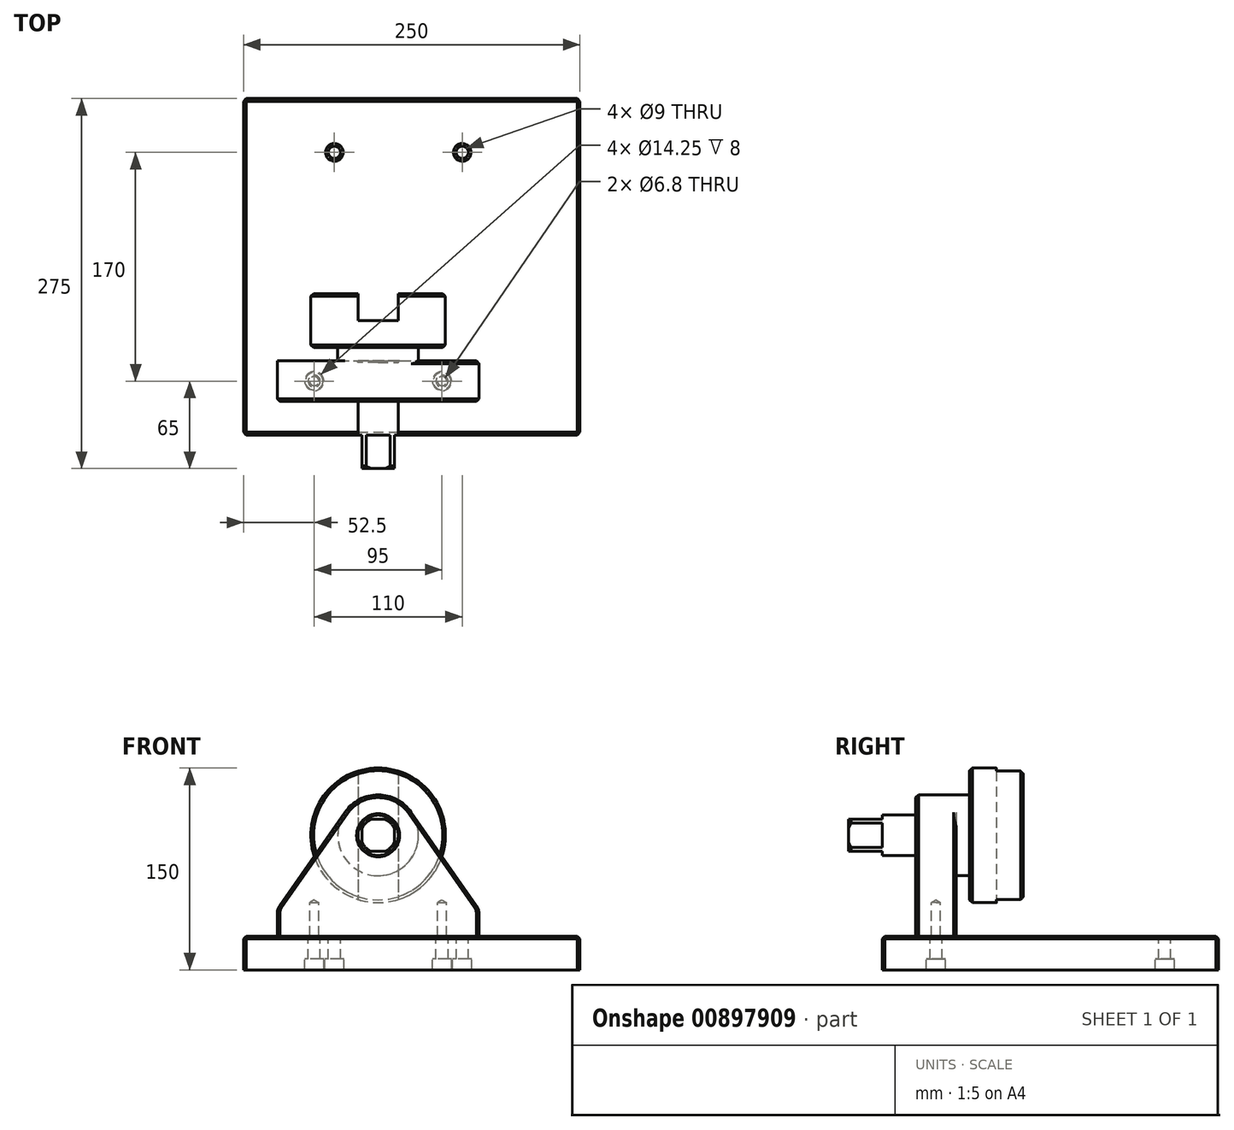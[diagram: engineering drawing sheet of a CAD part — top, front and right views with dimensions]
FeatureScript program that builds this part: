
annotation { "Feature Type Name" : "Feature", "Feature Type Description" : "" }
export const myFeature = defineFeature(function(context is Context, id is Id, definition is map)
    precondition{}
    {
        {
            var Q0;
            Q0=qCreatedBy(makeId("Top.planeOp"),FACE);
            cPlane(context, id + "F0", {"entities" : qUnion([Q0]), "cplaneType" : CPlaneType.OFFSET, "offset" : 25 * mm, "oppositeDirection" : true, "width" : 150 * mm, "height" : 150 * mm});
        }
        {
            var Q0;
            Q0=qCreatedBy(makeId("Front.planeOp"),FACE);
            var sketch = newSketch(context, id + "F1", { "sketchPlane" : qUnion([Q0])});
            skArc(sketch, "E0", {"start": v(24.6, 92.18) * mm, "mid": v(0, 105) * mm, "end": v(-24.6, 92.18) * mm});
            skLineSegment(sketch, "E1", {"start": v(-24.6, 92.18) * mm, "end": v(-75, 20) * mm});
            skLineSegment(sketch, "E2", {"start": v(-75, 20) * mm, "end": v(-75, 0) * mm});
            skLineSegment(sketch, "E3", {"start": v(-75, 0) * mm, "end": v(75, 0) * mm});
            skLineSegment(sketch, "E4", {"start": v(75, 0) * mm, "end": v(75, 20) * mm});
            skLineSegment(sketch, "E5", {"start": v(75, 20) * mm, "end": v(24.6, 92.18) * mm});
            skCircle(sketch, "E6", {"center": v(0, 75) * mm, "radius": 15 * mm});
            skSolve(sketch);
        }
        {
            var Q0;
            Q0=makeQuery(id+"F1.imprint","IMPRINT",FACE,{"disambiguationData":[TD([[makeQuery(id+"F1.imprint","IMPRINT",EDGE,{"derivedFrom":sQuery(id+"F1.wireOp",EDGE,"E0")}),1.0]])]});
            extrude(context, id + "F2", {"entities" : qUnion([Q0]), "depth" : 30 * mm, "offsetDistance" : 25 * mm});
        }
        {
            var Q0;
            Q0=makeQuery(id+"F2.opExtrude","SWEPT_EDGE",EDGE,{"disambiguationData":[OSD([sQuery(id+"F1.wireOp",EDGE,"E4"),sQuery(id+"F1.wireOp",EDGE,"E5")])]});
            var Q1;
            Q1=makeQuery(id+"F2.opExtrude","SWEPT_EDGE",EDGE,{"disambiguationData":[OSD([sQuery(id+"F1.wireOp",EDGE,"E1"),sQuery(id+"F1.wireOp",EDGE,"E2")])]});
            fillet(context, id + "F3", {"entities" : qUnion([Q0, Q1]), "radius" : 10 * mm, "tangentPropagation" : true, "allowEdgeOverflow" : false});
        }
        {
            var Q0;
            Q0=makeQuery(id+"F2.opExtrude","CAP_EDGE",EDGE,{"disambiguationData":[OSD([sQuery(id+"F1.wireOp",EDGE,"E6")])],"isStart":false});
            var Q1;
            Q1=makeQuery(id+"F2.opExtrude","CAP_EDGE",EDGE,{"disambiguationData":[OSD([sQuery(id+"F1.wireOp",EDGE,"E6")])],"isStart":true});
            chamfer(context, id + "F4", {"entities" : qUnion([Q0, Q1]), "width" : 1 * mm, "tangentPropagation" : true});
        }
        {
            var Q0;
            Q0=qCreatedBy(makeId("Top.planeOp"),FACE);
            var sketch = newSketch(context, id + "F5", { "sketchPlane" : qUnion([Q0])});
            skLineSegment(sketch, "E7.bottom", {"start": v(-100, -55) * mm, "end": v(150, -55) * mm});
            skLineSegment(sketch, "E7.top", {"start": v(-100, 195) * mm, "end": v(150, 195) * mm});
            skLineSegment(sketch, "E7.left", {"start": v(-100, -55) * mm, "end": v(-100, 195) * mm});
            skLineSegment(sketch, "E7.right", {"start": v(150, -55) * mm, "end": v(150, 195) * mm});
            skLineSegment(sketch, "E8", {"start": v(0, 0) * mm, "end": v(15, 170) * mm, "construction": true});
            skSolve(sketch);
        }
        {
            var Q0;
            Q0=makeQuery(id+"F5.imprint","IMPRINT",FACE,{"disambiguationData":[TD([[makeQuery(id+"F5.imprint","IMPRINT",EDGE,{"derivedFrom":sQuery(id+"F5.wireOp",EDGE,"E7.bottom")}),1.0]])]});
            var Q1;
            Q1=qCreatedBy(id+"F0.planeOp",FACE);
            extrude(context, id + "F6", {"entities" : qUnion([Q0]), "endBound" : BoundingType.UP_TO_SURFACE, "oppositeDirection" : true, "depth" : 25 * mm, "endBoundEntityFace" : qUnion([Q1]), "offsetDistance" : 25 * mm});
        }
        {
            var Q0;
            Q0=qCreatedBy(id+"F0.planeOp",FACE);
            var sketch = newSketch(context, id + "F7", { "sketchPlane" : qUnion([Q0])});
            skLineSegment(sketch, "E9.0", {"start": v(-75, -30) * mm, "end": v(75, -30) * mm, "construction": true});
            skLineSegment(sketch, "E9.1", {"start": v(-75, 0) * mm, "end": v(75, 0) * mm, "construction": true});
            skLineSegment(sketch, "E9.2", {"start": v(-75, -30) * mm, "end": v(-75, 0) * mm, "construction": true});
            skLineSegment(sketch, "E9.3", {"start": v(75, -30) * mm, "end": v(75, 0) * mm, "construction": true});
            skLineSegment(sketch, "E10", {"start": v(-75, -15) * mm, "end": v(75, -15) * mm, "construction": true});
            skPoint(sketch, "E11", {"position": v(-47.5, -15) * mm});
            skPoint(sketch, "E12", {"position": v(47.5, -15) * mm});
            skLineSegment(sketch, "E13.0", {"start": v(0, 0) * mm, "end": v(15, 170) * mm, "construction": true});
            skLineSegment(sketch, "E14.bottom", {"start": v(90, 140) * mm, "end": v(-60, 140) * mm, "construction": true});
            skLineSegment(sketch, "E14.top", {"start": v(90, 170) * mm, "end": v(-60, 170) * mm, "construction": true});
            skLineSegment(sketch, "E14.left", {"start": v(90, 140) * mm, "end": v(90, 170) * mm, "construction": true});
            skLineSegment(sketch, "E14.right", {"start": v(-60, 140) * mm, "end": v(-60, 170) * mm, "construction": true});
            skLineSegment(sketch, "E15", {"start": v(90, 155) * mm, "end": v(-60, 155) * mm, "construction": true});
            skPoint(sketch, "E16", {"position": v(62.5, 155) * mm});
            skPoint(sketch, "E17", {"position": v(-32.5, 155) * mm});
            skLineSegment(sketch, "E18", {"start": v(15, 170) * mm, "end": v(15, 140) * mm, "construction": true});
            skSolve(sketch);
        }
        {
            var Q0;
            Q0=sQuery(id+"F7.wireOp",VERTEX,"E11");
            var Q1;
            Q1=sQuery(id+"F7.wireOp",VERTEX,"E12");
            var Q2;
            Q2=makeQuery(id+"F2.opExtrude","SWEPT_BODY",BODY,{"disambiguationData":[OSD([sQuery(id+"F1.wireOp",EDGE,"E0"),sQuery(id+"F1.wireOp",EDGE,"E1"),sQuery(id+"F1.wireOp",EDGE,"E2"),sQuery(id+"F1.wireOp",EDGE,"E3"),sQuery(id+"F1.wireOp",EDGE,"E4"),sQuery(id+"F1.wireOp",EDGE,"E5"),sQuery(id+"F1.wireOp",EDGE,"E6")])]});
            var Q3;
            Q3=makeQuery(id+"F6.opExtrude","SWEPT_BODY",BODY,{"disambiguationData":[OSD([sQuery(id+"F5.wireOp",EDGE,"E7.bottom"),sQuery(id+"F5.wireOp",EDGE,"E7.top"),sQuery(id+"F5.wireOp",EDGE,"E7.left"),sQuery(id+"F5.wireOp",EDGE,"E7.right")])]});
            hole(context, id + "F8", {"style" : HoleStyle.C_BORE, "endStyle" : HoleEndStyle.BLIND_IN_LAST, "oppositeDirection" : true, "standardTappedOrClearance" : lookupTablePath({ "fit" : "Normal", "standard" : "ISO", "engagement" : "75%", "pitch" : "1.25 mm", "size" : "M8", "type" : "Clearance & tapped" }), "standardBlindInLast" : lookupTablePath({ "fit" : "Normal", "standard" : "ISO", "engagement" : "75%", "pitch" : "1.25 mm", "size" : "M8", "type" : "Clearance & tapped" }), "holeDiameter" : 9 * mm, "cBoreDiameter" : 14.25 * mm, "cBoreDepth" : 8 * mm, "tapDrillDiameter" : 6.8 * mm, "majorDiameter" : 8 * mm, "showTappedDepth" : true, "holeDepth" : 25 * mm, "isTappedThrough" : true, "tappedDepth" : 21.25 * mm, "tapClearance" : 3, "startFromSketch" : true, "locations" : qUnion([Q0, Q1]), "scope" : qUnion([Q2, Q3])});
        }
        {
            var Q0;
            Q0=sQuery(id+"F7.wireOp",VERTEX,"E16");
            var Q1;
            Q1=sQuery(id+"F7.wireOp",VERTEX,"E17");
            var Q2;
            Q2=makeQuery(id+"F6.opExtrude","SWEPT_BODY",BODY,{"disambiguationData":[OSD([sQuery(id+"F5.wireOp",EDGE,"E7.bottom"),sQuery(id+"F5.wireOp",EDGE,"E7.top"),sQuery(id+"F5.wireOp",EDGE,"E7.left"),sQuery(id+"F5.wireOp",EDGE,"E7.right")])]});
            hole(context, id + "F9", {"style" : HoleStyle.C_BORE, "endStyle" : HoleEndStyle.THROUGH, "oppositeDirection" : true, "standardTappedOrClearance" : lookupTablePath({ "fit" : "Normal", "standard" : "ISO", "size" : "M8", "type" : "Clearance" }), "standardBlindInLast" : lookupTablePath({ "fit" : "Normal", "standard" : "ISO", "size" : "M8", "type" : "Clearance" }), "holeDiameter" : 9 * mm, "cBoreDiameter" : 14.25 * mm, "cBoreDepth" : 8 * mm, "majorDiameter" : 8 * mm, "isTappedThrough" : true, "tappedDepth" : 21.25 * mm, "tapClearance" : 3, "startFromSketch" : true, "locations" : qUnion([Q0, Q1]), "scope" : qUnion([Q2])});
        }
        {
            var Q0;
            Q0=makeQuery(id+"F2.opExtrude","CAP_FACE",FACE,{"disambiguationData":[OSD([sQuery(id+"F1.wireOp",EDGE,"E0"),sQuery(id+"F1.wireOp",EDGE,"E1"),sQuery(id+"F1.wireOp",EDGE,"E2"),sQuery(id+"F1.wireOp",EDGE,"E3"),sQuery(id+"F1.wireOp",EDGE,"E4"),sQuery(id+"F1.wireOp",EDGE,"E5"),sQuery(id+"F1.wireOp",EDGE,"E6")])],"isStart":true});
            var sketch = newSketch(context, id + "F10", { "sketchPlane" : qUnion([Q0])});
            skCircle(sketch, "E19.0", {"center": v(0, 75) * mm, "radius": 15 * mm});
            skCircle(sketch, "E20", {"center": v(0, 75) * mm, "radius": 50 * mm});
            skCircle(sketch, "E21", {"center": v(0, 75) * mm, "radius": 30 * mm});
            skSolve(sketch);
        }
        {
            var Q0;
            Q0=makeQuery(id+"F10.imprint","IMPRINT",FACE,{"disambiguationData":[TD([[makeQuery(id+"F10.imprint","IMPRINT",EDGE,{"derivedFrom":sQuery(id+"F10.wireOp",EDGE,"E19.0")}),1.0]])]});
            extrude(context, id + "F11", {"entities" : qUnion([Q0]), "oppositeDirection" : true, "depth" : 80 * mm, "offsetDistance" : 25 * mm});
        }
        {
            var Q0;
            {var subQ0=sQuery(id+"F10.wireOp",EDGE,"E21");Q0=makeQuery(id+"F10.imprint","IMPRINT",FACE,{"disambiguationData":[TD([[makeQuery(id+"F10.imprint","IMPRINT",EDGE,{"disambiguationData":[OD(0.0)],"derivedFrom":subQ0}),-1.0]])]});}
            var Q1;
            Q1=makeQuery(id+"F10.imprint","IMPRINT",FACE,{"disambiguationData":[TD([[makeQuery(id+"F10.imprint","IMPRINT",EDGE,{"derivedFrom":sQuery(id+"F10.wireOp",EDGE,"E19.0")}),-1.0]])]});
            var Q2;
            Q2=makeQuery(id+"F10.imprint","IMPRINT",FACE,{"disambiguationData":[TD([[makeQuery(id+"F10.imprint","IMPRINT",EDGE,{"derivedFrom":sQuery(id+"F10.wireOp",EDGE,"E19.0")}),1.0]])]});
            extrude(context, id + "F12", {"entities" : qUnion([Q0, Q1, Q2]), "operationType" : NewBodyOperationType.ADD, "depth" : 10 * mm, "offsetDistance" : 25 * mm});
        }
        {
            var Q0;
            Q0=makeQuery(id+"F10.imprint","IMPRINT",FACE,{"disambiguationData":[TD([[makeQuery(id+"F10.imprint","IMPRINT",EDGE,{"derivedFrom":sQuery(id+"F10.wireOp",EDGE,"E19.0")}),1.0]])]});
            var Q1;
            {var subQ0=sQuery(id+"F10.wireOp",EDGE,"E21");Q1=makeQuery(id+"F10.imprint","IMPRINT",FACE,{"disambiguationData":[TD([[makeQuery(id+"F10.imprint","IMPRINT",EDGE,{"disambiguationData":[OD(0.0)],"derivedFrom":subQ0}),-1.0]])]});}
            var Q2;
            Q2=makeQuery(id+"F10.imprint","IMPRINT",FACE,{"disambiguationData":[TD([[makeQuery(id+"F10.imprint","IMPRINT",EDGE,{"derivedFrom":sQuery(id+"F10.wireOp",EDGE,"E19.0")}),-1.0]])]});
            var Q3;
            {var subQ5=sQuery(id+"F10.wireOp",EDGE,"E21");Q3=makeQuery(id+"F10.imprint","IMPRINT",FACE,{"disambiguationData":[TD([[makeQuery(id+"F10.imprint","IMPRINT",EDGE,{"disambiguationData":[OD(0.0)],"derivedFrom":subQ5}),1.0]])]});}
            var Q4;
            {var subQ5=sQuery(id+"F10.wireOp",EDGE,"E21");Q4=makeQuery(id+"F10.imprint","IMPRINT",FACE,{"disambiguationData":[TD([[makeQuery(id+"F10.imprint","IMPRINT",EDGE,{"disambiguationData":[OD(1.0)],"derivedFrom":subQ5}),-1.0]])]});}
            extrude(context, id + "F13", {"entities" : qUnion([Q0, Q1, Q2, Q3, Q4]), "operationType" : NewBodyOperationType.ADD, "depth" : 50 * mm, "offsetDistance" : 25 * mm, "hasSecondDirection" : true, "secondDirectionOppositeDirection" : true, "secondDirectionDepth" : -10 * mm});
        }
        {
            var Q0;
            Q0=makeQuery(id+"F13.opExtrude","CAP_FACE",FACE,{"disambiguationData":[OSD([sQuery(id+"F10.wireOp",EDGE,"E20")])],"isStart":false});
            var sketch = newSketch(context, id + "F14", { "sketchPlane" : qUnion([Q0])});
            skLineSegment(sketch, "E22.bottom", {"start": v(-15, 125) * mm, "end": v(15, 125) * mm});
            skLineSegment(sketch, "E22.top", {"start": v(-15, 25) * mm, "end": v(15, 25) * mm});
            skLineSegment(sketch, "E22.left", {"start": v(-15, 125) * mm, "end": v(-15, 25) * mm});
            skLineSegment(sketch, "E22.right", {"start": v(15, 125) * mm, "end": v(15, 25) * mm});
            skSolve(sketch);
        }
        {
            var Q0;
            Q0 = qSketchRegion(id + "F14", true);
            extrude(context, id + "F15", {"entities" : qUnion([Q0]), "operationType" : NewBodyOperationType.REMOVE, "oppositeDirection" : true, "depth" : 20 * mm, "offsetDistance" : 25 * mm});
        }
        {
            var Q0;
            Q0=makeQuery(id+"F15.boolean.opBoolean","COPY",EDGE,{"derivedFrom":makeQuery(id+"F15.opExtrude","CAP_EDGE",EDGE,{"disambiguationData":[OSD([sQuery(id+"F14.wireOp",EDGE,"E22.right")])],"isStart":true})});
            var Q1;
            Q1=makeQuery(id+"F15.boolean.opBoolean","COPY",EDGE,{"derivedFrom":makeQuery(id+"F15.opExtrude","CAP_EDGE",EDGE,{"disambiguationData":[OSD([sQuery(id+"F14.wireOp",EDGE,"E22.left")])],"isStart":true})});
            var Q2;
            Q2=makeQuery(id+"F13.opExtrude","CAP_EDGE",EDGE,{"disambiguationData":[OSD([sQuery(id+"F10.wireOp",EDGE,"E20")])],"isStart":true});
            var Q3;
            Q3=makeQuery(id+"F12.opExtrude","CAP_EDGE",EDGE,{"disambiguationData":[OSD([sQuery(id+"F10.wireOp",EDGE,"E21")])],"isStart":true});
            var Q4;
            Q4=makeQuery(id+"F11.opExtrude","CAP_EDGE",EDGE,{"disambiguationData":[OSD([sQuery(id+"F10.wireOp",EDGE,"E19.0")])],"isStart":false});
            var Q5;
            {var subQ0=sQuery(id+"F10.wireOp",EDGE,"E20");Q5=makeQuery(id+"F15.boolean.opBoolean","SPLIT",EDGE,{"disambiguationData":[TD([makeQuery(id+"F15.opExtrude","SWEPT_FACE",FACE,{"disambiguationData":[OSD([sQuery(id+"F14.wireOp",EDGE,"E22.right")])]})])],"derivedFrom":makeQuery(id+"F13.opExtrude","CAP_EDGE",EDGE,{"disambiguationData":[OSD([subQ0])],"isStart":false})});}
            var Q6;
            {var subQ0=sQuery(id+"F10.wireOp",EDGE,"E20");Q6=makeQuery(id+"F15.boolean.opBoolean","SPLIT",EDGE,{"disambiguationData":[TD([makeQuery(id+"F15.opExtrude","SWEPT_FACE",FACE,{"disambiguationData":[OSD([sQuery(id+"F14.wireOp",EDGE,"E22.left")])]})])],"derivedFrom":makeQuery(id+"F13.opExtrude","CAP_EDGE",EDGE,{"disambiguationData":[OSD([subQ0])],"isStart":false})});}
            chamfer(context, id + "F16", {"entities" : qUnion([Q0, Q1, Q2, Q3, Q4, Q5, Q6]), "width" : 2 * mm, "tangentPropagation" : true});
        }
        {
            var Q0;
            Q0=makeQuery(id+"F11.opExtrude","CAP_FACE",FACE,{"disambiguationData":[OSD([sQuery(id+"F10.wireOp",EDGE,"E19.0")])],"isStart":false});
            var sketch = newSketch(context, id + "F17", { "sketchPlane" : qUnion([Q0])});
            skLineSegment(sketch, "E23.bottom", {"start": v(12, 63) * mm, "end": v(-12, 63) * mm});
            skLineSegment(sketch, "E23.top", {"start": v(12, 87) * mm, "end": v(-12, 87) * mm});
            skLineSegment(sketch, "E23.left", {"start": v(12, 63) * mm, "end": v(12, 87) * mm});
            skLineSegment(sketch, "E23.right", {"start": v(-12, 63) * mm, "end": v(-12, 87) * mm});
            skPoint(sketch, "E23.middle", {"position": v(0, 75) * mm});
            skLineSegment(sketch, "E24.bottom", {"start": v(17, 58) * mm, "end": v(-17, 58) * mm});
            skLineSegment(sketch, "E24.top", {"start": v(17, 92) * mm, "end": v(-17, 92) * mm});
            skLineSegment(sketch, "E24.left", {"start": v(17, 58) * mm, "end": v(17, 92) * mm});
            skLineSegment(sketch, "E24.right", {"start": v(-17, 58) * mm, "end": v(-17, 92) * mm});
            skSolve(sketch);
        }
        {
            var Q0;
            Q0 = qSketchRegion(id + "F17", true);
            extrude(context, id + "F18", {"entities" : qUnion([Q0]), "operationType" : NewBodyOperationType.REMOVE, "oppositeDirection" : true, "depth" : 25 * mm, "offsetDistance" : 25 * mm});
        }
        {
            var Q0;
            Q0=makeQuery(id+"F6.opExtrude","CAP_FACE",FACE,{"disambiguationData":[OSD([sQuery(id+"F5.wireOp",EDGE,"E7.bottom"),sQuery(id+"F5.wireOp",EDGE,"E7.top"),sQuery(id+"F5.wireOp",EDGE,"E7.left"),sQuery(id+"F5.wireOp",EDGE,"E7.right")])],"isStart":true});
            var Q1;
            Q1=makeQuery(id+"F6.opExtrude","SWEPT_EDGE",EDGE,{"disambiguationData":[OSD([sQuery(id+"F5.wireOp",EDGE,"E7.top"),sQuery(id+"F5.wireOp",EDGE,"E7.right")])]});
            var Q2;
            Q2=makeQuery(id+"F6.opExtrude","SWEPT_EDGE",EDGE,{"disambiguationData":[OSD([sQuery(id+"F5.wireOp",EDGE,"E7.top"),sQuery(id+"F5.wireOp",EDGE,"E7.left")])]});
            var Q3;
            Q3=makeQuery(id+"F6.opExtrude","SWEPT_EDGE",EDGE,{"disambiguationData":[OSD([sQuery(id+"F5.wireOp",EDGE,"E7.bottom"),sQuery(id+"F5.wireOp",EDGE,"E7.right")])]});
            var Q4;
            Q4=makeQuery(id+"F6.opExtrude","SWEPT_EDGE",EDGE,{"disambiguationData":[OSD([sQuery(id+"F5.wireOp",EDGE,"E7.bottom"),sQuery(id+"F5.wireOp",EDGE,"E7.left")])]});
            chamfer(context, id + "F19", {"entities" : qUnion([Q0, Q1, Q2, Q3, Q4]), "width" : 2 * mm, "tangentPropagation" : true});
        }
        {
            var Q0;
            Q0=makeQuery(id+"F2.opExtrude","CAP_EDGE",EDGE,{"disambiguationData":[OSD([sQuery(id+"F1.wireOp",EDGE,"E5")])],"isStart":false});
            var Q1;
            Q1=makeQuery(id+"F2.opExtrude","CAP_EDGE",EDGE,{"disambiguationData":[OSD([sQuery(id+"F1.wireOp",EDGE,"E5")])],"isStart":true});
            chamfer(context, id + "F20", {"entities" : qUnion([Q0, Q1]), "width" : 2 * mm, "tangentPropagation" : true});
        }
    });
